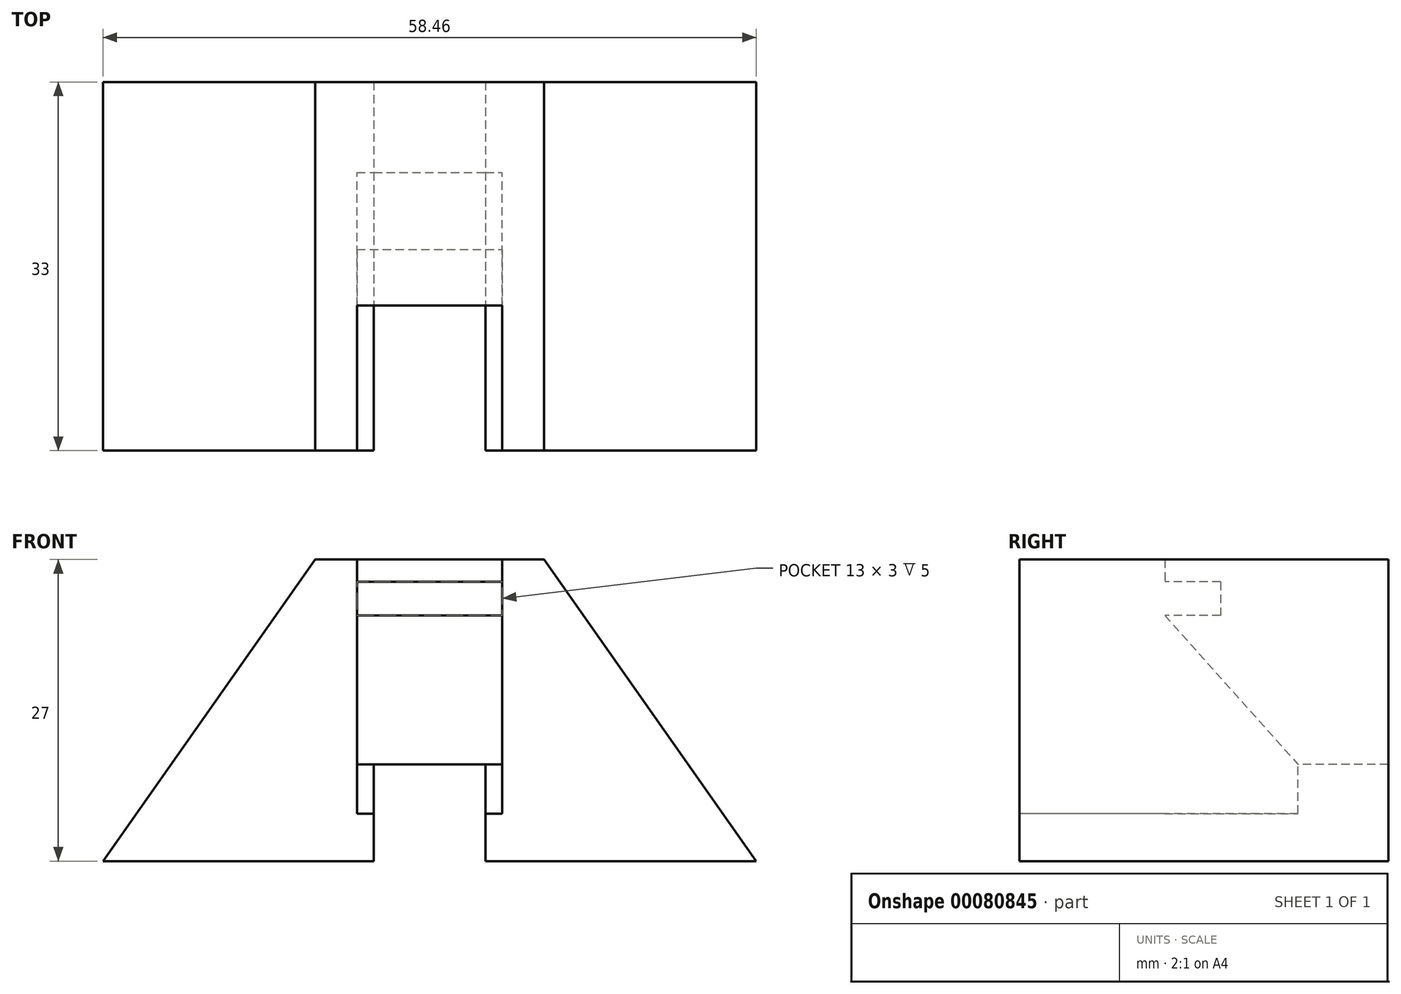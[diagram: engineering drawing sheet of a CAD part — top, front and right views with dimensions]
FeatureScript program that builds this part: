
annotation { "Feature Type Name" : "Feature", "Feature Type Description" : "" }
export const myFeature = defineFeature(function(context is Context, id is Id, definition is map)
    precondition{}
    {
        {
            var Q0;
            Q0=qCreatedBy(makeId("Top.planeOp"),FACE);
            var sketch = newSketch(context, id + "F0", { "sketchPlane" : qUnion([Q0])});
            skLineSegment(sketch, "E0.bottom", {"start": v(-29.22, 16.5) * mm, "end": v(29.23, 16.5) * mm});
            skLineSegment(sketch, "E0.top", {"start": v(-29.23, -16.5) * mm, "end": v(29.23, -16.5) * mm});
            skLineSegment(sketch, "E0.left", {"start": v(-29.23, 16.5) * mm, "end": v(-29.23, -16.5) * mm});
            skLineSegment(sketch, "E0.right", {"start": v(29.23, 16.5) * mm, "end": v(29.23, -16.5) * mm});
            skSolve(sketch);
        }
        {
            var Q0;
            Q0 = qSketchRegion(id + "F0", true);
            extrude(context, id + "F1", {"entities" : qUnion([Q0]), "depth" : 27 * mm});
        }
        {
            var Q0;
            Q0=makeQuery(id+"F1.opExtrude","SWEPT_FACE",FACE,{"disambiguationData":[OSD([sQuery(id+"F0.wireOp",EDGE,"E0.top")])]});
            var sketch = newSketch(context, id + "F2", { "sketchPlane" : qUnion([Q0])});
            skLineSegment(sketch, "E1", {"start": v(-29.23, 0) * mm, "end": v(-10.25, 27) * mm});
            skLineSegment(sketch, "E2", {"start": v(29.22, 0) * mm, "end": v(10.25, 27) * mm});
            skSolve(sketch);
        }
        {
            var Q0;
            Q0 = qSketchRegion(id + "F2", true);
            var Q1;
            {var subQ0=sQuery(id+"F2.wireOp",EDGE,"E1");Q1=makeQuery(id+"F2.imprint","IMPRINT",FACE,{"disambiguationData":[TD([[makeQuery(id+"F2.imprint","IMPRINT",EDGE,{"derivedFrom":subQ0}),1.0]])]});}
            var Q2;
            {var subQ0=sQuery(id+"F2.wireOp",EDGE,"E2");Q2=makeQuery(id+"F2.imprint","IMPRINT",FACE,{"disambiguationData":[TD([[makeQuery(id+"F2.imprint","IMPRINT",EDGE,{"derivedFrom":subQ0}),-1.0]])]});}
            extrude(context, id + "F3", {"entities" : qUnion([Q0, Q1, Q2]), "operationType" : NewBodyOperationType.REMOVE, "endBound" : BoundingType.THROUGH_ALL, "oppositeDirection" : true, "depth" : 25 * mm});
        }
        {
            var Q0;
            Q0=makeQuery(id+"F1.opExtrude","SWEPT_FACE",FACE,{"disambiguationData":[OSD([sQuery(id+"F0.wireOp",EDGE,"E0.top")])]});
            var sketch = newSketch(context, id + "F4", { "sketchPlane" : qUnion([Q0])});
            skLineSegment(sketch, "E3.bottom", {"start": v(-5, 8.67) * mm, "end": v(5, 8.67) * mm});
            skLineSegment(sketch, "E3.top", {"start": v(-5, 0) * mm, "end": v(5, 0) * mm});
            skLineSegment(sketch, "E3.left", {"start": v(-5, 8.67) * mm, "end": v(-5, 0) * mm});
            skLineSegment(sketch, "E3.right", {"start": v(5, 8.67) * mm, "end": v(5, 0) * mm});
            skSolve(sketch);
        }
        {
            var Q0;
            Q0 = qSketchRegion(id + "F4", true);
            extrude(context, id + "F5", {"entities" : qUnion([Q0]), "operationType" : NewBodyOperationType.REMOVE, "endBound" : BoundingType.THROUGH_ALL, "oppositeDirection" : true, "depth" : 25 * mm});
        }
        {
            var Q0;
            Q0=makeQuery(id+"F1.opExtrude","SWEPT_FACE",FACE,{"disambiguationData":[OSD([sQuery(id+"F0.wireOp",EDGE,"E0.top")])]});
            var sketch = newSketch(context, id + "F6", { "sketchPlane" : qUnion([Q0])});
            skLineSegment(sketch, "E4.bottom", {"start": v(-6.5, 27) * mm, "end": v(6.5, 27) * mm});
            skLineSegment(sketch, "E4.top", {"start": v(-6.5, 4.25) * mm, "end": v(6.5, 4.25) * mm});
            skLineSegment(sketch, "E4.left", {"start": v(-6.5, 27) * mm, "end": v(-6.5, 4.25) * mm});
            skLineSegment(sketch, "E4.right", {"start": v(6.5, 27) * mm, "end": v(6.5, 4.25) * mm});
            skSolve(sketch);
        }
        {
            var Q0;
            Q0 = qSketchRegion(id + "F6", true);
            extrude(context, id + "F7", {"entities" : qUnion([Q0]), "operationType" : NewBodyOperationType.REMOVE, "oppositeDirection" : true, "depth" : 13 * mm});
        }
        {
            var Q0;
            Q0=makeQuery(id+"F7.boolean.opBoolean","COPY",FACE,{"derivedFrom":makeQuery(id+"F7.opExtrude","CAP_FACE",FACE,{"disambiguationData":[OSD([sQuery(id+"F6.wireOp",EDGE,"E4.bottom"),sQuery(id+"F6.wireOp",EDGE,"E4.top"),sQuery(id+"F6.wireOp",EDGE,"E4.left"),sQuery(id+"F6.wireOp",EDGE,"E4.right")])],"isStart":false})});
            var sketch = newSketch(context, id + "F8", { "sketchPlane" : qUnion([Q0])});
            skLineSegment(sketch, "E5.bottom", {"start": v(-6.5, 25) * mm, "end": v(6.5, 25) * mm});
            skLineSegment(sketch, "E5.top", {"start": v(-6.5, 22) * mm, "end": v(6.5, 22) * mm});
            skLineSegment(sketch, "E5.left", {"start": v(-6.5, 25) * mm, "end": v(-6.5, 22) * mm});
            skLineSegment(sketch, "E5.right", {"start": v(6.5, 25) * mm, "end": v(6.5, 22) * mm});
            skSolve(sketch);
        }
        {
            var Q0;
            Q0 = qSketchRegion(id + "F8", true);
            extrude(context, id + "F9", {"entities" : qUnion([Q0]), "operationType" : NewBodyOperationType.REMOVE, "oppositeDirection" : true, "depth" : 5 * mm});
        }
        {
            var Q0;
            Q0=qCreatedBy(makeId("Right.planeOp"),FACE);
            var sketch = newSketch(context, id + "F10", { "sketchPlane" : qUnion([Q0])});
            skLineSegment(sketch, "E6", {"start": v(-3.5, 22) * mm, "end": v(-3.5, 4.25) * mm});
            skLineSegment(sketch, "E7", {"start": v(-3.5, 22) * mm, "end": v(8.41, 8.67) * mm});
            skLineSegment(sketch, "E8", {"start": v(-3.5, 4.25) * mm, "end": v(8.41, 4.25) * mm});
            skLineSegment(sketch, "E9", {"start": v(8.41, 8.67) * mm, "end": v(8.41, 4.25) * mm});
            skSolve(sketch);
        }
        {
            var Q0;
            Q0 = qSketchRegion(id + "F10", true);
            extrude(context, id + "F11", {"entities" : qUnion([Q0]), "operationType" : NewBodyOperationType.REMOVE, "endBound" : BoundingType.SYMMETRIC, "oppositeDirection" : true, "depth" : 13 * mm});
        }
    });
